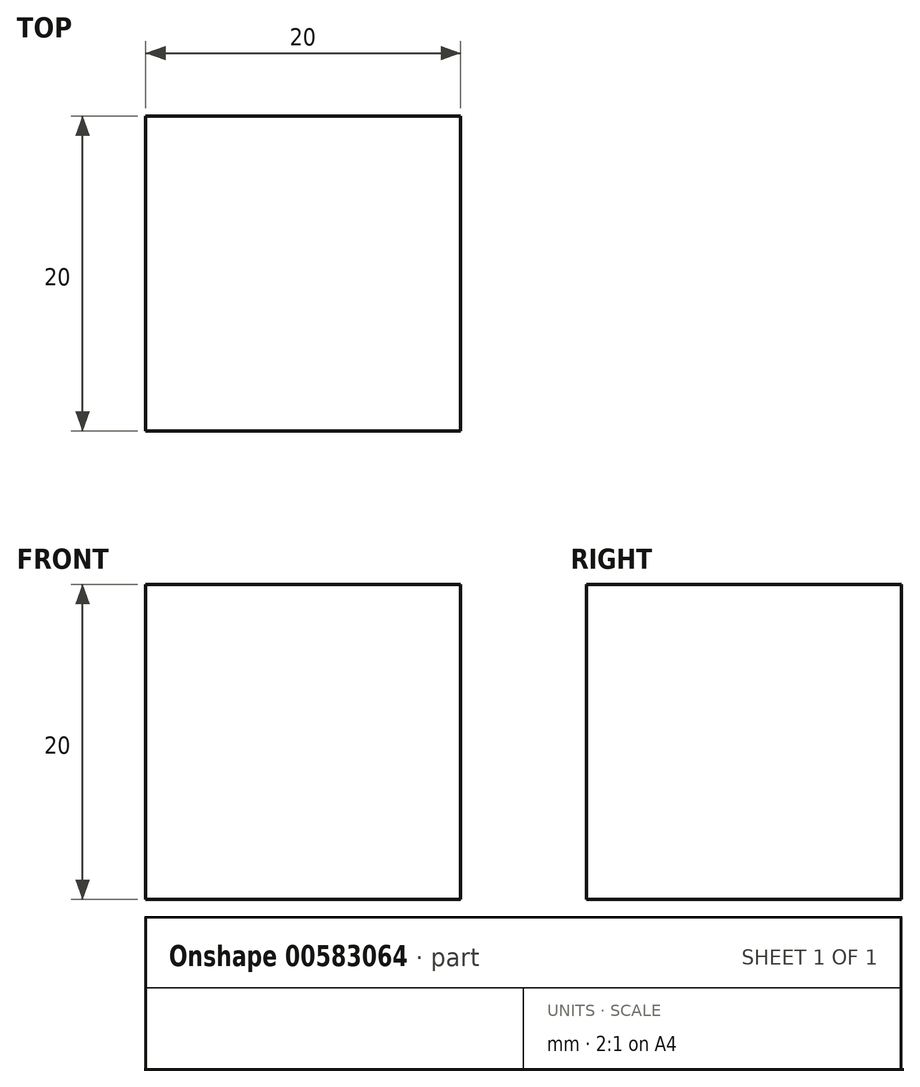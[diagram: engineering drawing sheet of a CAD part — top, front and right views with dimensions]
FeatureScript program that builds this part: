
annotation { "Feature Type Name" : "Feature", "Feature Type Description" : "" }
export const myFeature = defineFeature(function(context is Context, id is Id, definition is map)
    precondition{}
    {
        {
            var Q0;
            Q0=qCreatedBy(makeId("Front.planeOp"),FACE);
            var sketch = newSketch(context, id + "F0", { "sketchPlane" : qUnion([Q0])});
            skLineSegment(sketch, "E0.bottom", {"start": v(0, 0) * mm, "end": v(-20, 0) * mm});
            skLineSegment(sketch, "E0.top", {"start": v(0, 20) * mm, "end": v(-20, 20) * mm});
            skLineSegment(sketch, "E0.left", {"start": v(0, 0) * mm, "end": v(0, 20) * mm});
            skLineSegment(sketch, "E0.right", {"start": v(-20, 0) * mm, "end": v(-20, 20) * mm});
            skSolve(sketch);
        }
        {
            var Q0;
            Q0=makeQuery(id+"F0.imprint","IMPRINT",FACE,{"disambiguationData":[TD([[makeQuery(id+"F0.imprint","IMPRINT",EDGE,{"derivedFrom":sQuery(id+"F0.wireOp",EDGE,"E0.bottom")}),-1.0]])]});
            extrude(context, id + "F1", {"entities" : qUnion([Q0]), "depth" : 20 * mm, "offsetDistance" : 25 * mm});
        }
    });
